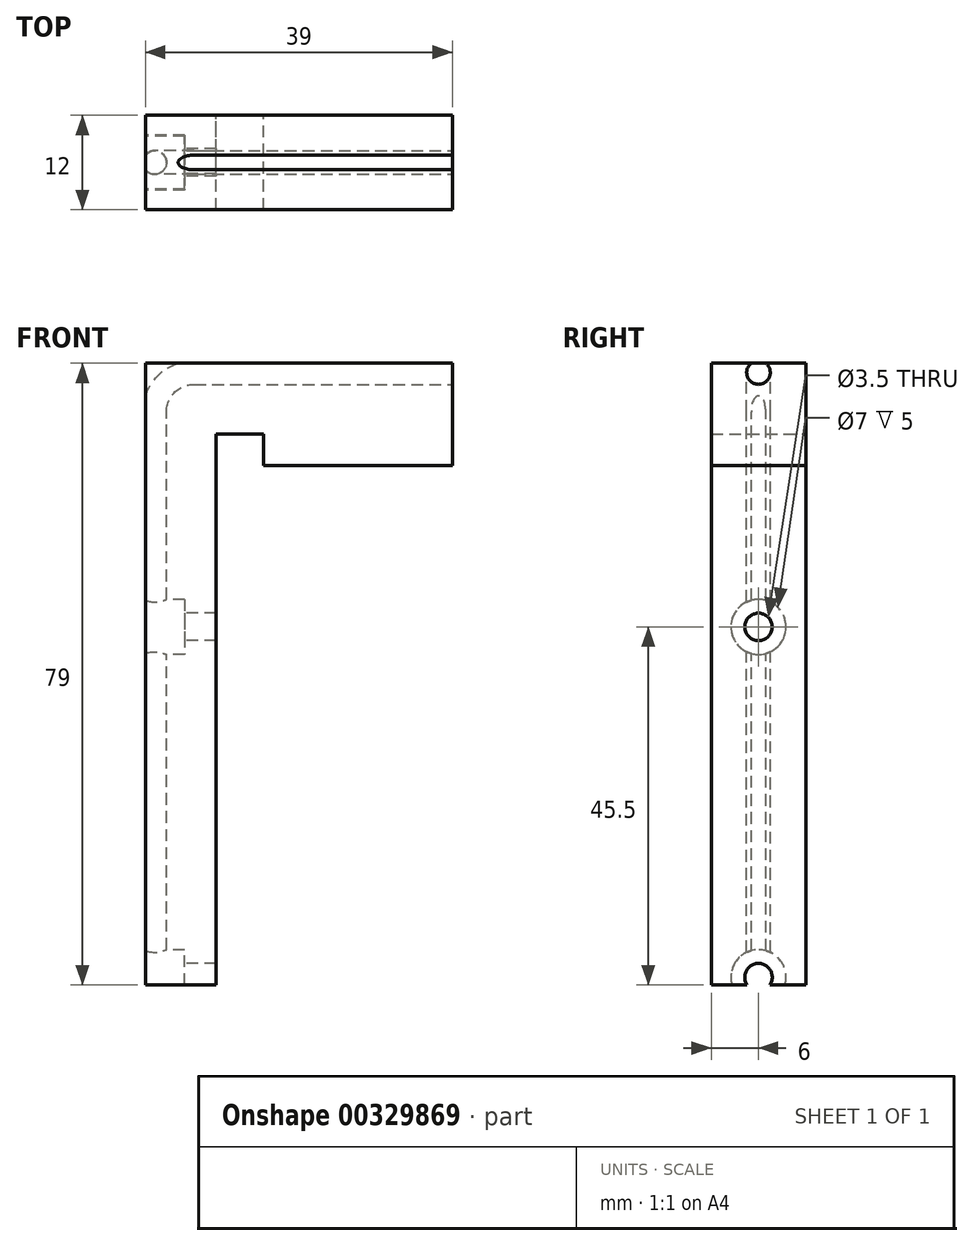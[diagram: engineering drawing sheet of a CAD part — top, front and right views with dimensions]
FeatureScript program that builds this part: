
annotation { "Feature Type Name" : "Feature", "Feature Type Description" : "" }
export const myFeature = defineFeature(function(context is Context, id is Id, definition is map)
    precondition{}
    {
        {
            assignVariable(context, id + "F0", {"name" : "Guide_Diam", "anyValue" : 3});
        }
        {
            var Q0;
            Q0=qCreatedBy(makeId("Front.planeOp"),FACE);
            var sketch = newSketch(context, id + "F1", { "sketchPlane" : qUnion([Q0])});
            skLineSegment(sketch, "E0", {"start": v(0, 0) * mm, "end": v(0, 70) * mm});
            skLineSegment(sketch, "E1", {"start": v(0, 70) * mm, "end": v(6, 70) * mm});
            skLineSegment(sketch, "E2", {"start": v(30, 79) * mm, "end": v(-9, 79) * mm});
            skLineSegment(sketch, "E3", {"start": v(-9, 79) * mm, "end": v(-9, 0) * mm});
            skLineSegment(sketch, "E4", {"start": v(-9, 0) * mm, "end": v(0, 0) * mm});
            skLineSegment(sketch, "E5", {"start": v(6, 70) * mm, "end": v(6, 66) * mm});
            skLineSegment(sketch, "E6", {"start": v(6, 66) * mm, "end": v(30, 66) * mm});
            skLineSegment(sketch, "E7", {"start": v(30, 66) * mm, "end": v(30, 79) * mm});
            skSolve(sketch);
        }
        {
            var Q0;
            Q0 = qSketchRegion(id + "F1", true);
            extrude(context, id + "F2", {"entities" : qUnion([Q0]), "depth" : 12 * mm, "offsetDistance" : 25 * mm, "symmetric" : true});
        }
        {
            var Q0;
            Q0=makeQuery(id+"F2.opExtrude","SWEPT_FACE",FACE,{"disambiguationData":[OSD([sQuery(id+"F1.wireOp",EDGE,"E4")])]});
            var sketch = newSketch(context, id + "F3", { "sketchPlane" : qUnion([Q0])});
            skCircle(sketch, "E8", {"center": v(-7.82, 0) * mm, "radius": 1.5 * mm});
            skPoint(sketch, "E9", {"position": v(-9, 0.93) * mm});
            skPoint(sketch, "E10", {"position": v(-9, -0.93) * mm});
            skSolve(sketch);
        }
        {
            var Q0;
            Q0=qCreatedBy(makeId("Front.planeOp"),FACE);
            var sketch = newSketch(context, id + "F4", { "sketchPlane" : qUnion([Q0])});
            skLineSegment(sketch, "E11", {"start": v(-7.82, 0) * mm, "end": v(-7.82, 72.82) * mm});
            skLineSegment(sketch, "E12", {"start": v(30, 77.82) * mm, "end": v(-2.82, 77.82) * mm});
            skLineSegment(sketch, "E13", {"start": v(-7.82, 0) * mm, "end": v(-9, 0) * mm, "construction": true});
            skLineSegment(sketch, "E14", {"start": v(30, 77.82) * mm, "end": v(30, 79) * mm, "construction": true});
            skPoint(sketch, "E15.visualSharp", {"position": v(-7.82, 77.82) * mm});
            skArc(sketch, "E15.filletArc", {"start": v(-2.82, 77.82) * mm, "mid": v(-6.35, 76.35) * mm, "end": v(-7.82, 72.82) * mm});
            skSolve(sketch);
        }
        {
            var Q0;
            Q0 = qSketchRegion(id + "F3", true);
            var Q1;
            Q1 = qConstructionFilter(qBodyType(qCreatedBy(id + "F4" ,EDGE), BodyType.WIRE), ConstructionObject.NO);
            sweep(context, id + "F5", {"operationType" : NewBodyOperationType.REMOVE, "profiles" : qUnion([Q0]), "path" : qUnion([Q1])});
        }
        {
            var Q0;
            Q0=makeQuery(id+"F2.opExtrude","SWEPT_FACE",FACE,{"disambiguationData":[OSD([sQuery(id+"F1.wireOp",EDGE,"E3")])]});
            var sketch = newSketch(context, id + "F6", { "sketchPlane" : qUnion([Q0])});
            skCircle(sketch, "E16", {"center": v(0, 45.5) * mm, "radius": 1.75 * mm});
            skCircle(sketch, "E17", {"center": v(0, 1) * mm, "radius": 1.75 * mm});
            skSolve(sketch);
        }
        {
            var Q0;
            Q0 = qSketchRegion(id + "F6", true);
            var Q1;
            Q1=makeQuery(id+"F2.opExtrude","SWEPT_FACE",FACE,{"disambiguationData":[OSD([sQuery(id+"F1.wireOp",EDGE,"E0")])]});
            extrude(context, id + "F7", {"entities" : qUnion([Q0]), "operationType" : NewBodyOperationType.REMOVE, "endBound" : BoundingType.UP_TO_SURFACE, "oppositeDirection" : true, "depth" : 25 * mm, "endBoundEntityFace" : qUnion([Q1]), "offsetDistance" : 25 * mm});
        }
        {
            var Q0;
            Q0=makeQuery(id+"F2.opExtrude","SWEPT_FACE",FACE,{"disambiguationData":[OSD([sQuery(id+"F1.wireOp",EDGE,"E3")])]});
            var sketch = newSketch(context, id + "F8", { "sketchPlane" : qUnion([Q0])});
            skCircle(sketch, "E18", {"center": v(0, 45.5) * mm, "radius": 3.5 * mm});
            skCircle(sketch, "E19", {"center": v(0, 1) * mm, "radius": 3.5 * mm});
            skSolve(sketch);
        }
        {
            var Q0;
            Q0 = qSketchRegion(id + "F8", true);
            extrude(context, id + "F9", {"entities" : qUnion([Q0]), "operationType" : NewBodyOperationType.REMOVE, "oppositeDirection" : true, "depth" : (getVariable(context, 'Guide_Diam') + 2) * mm, "offsetDistance" : 25 * mm});
        }
    });
